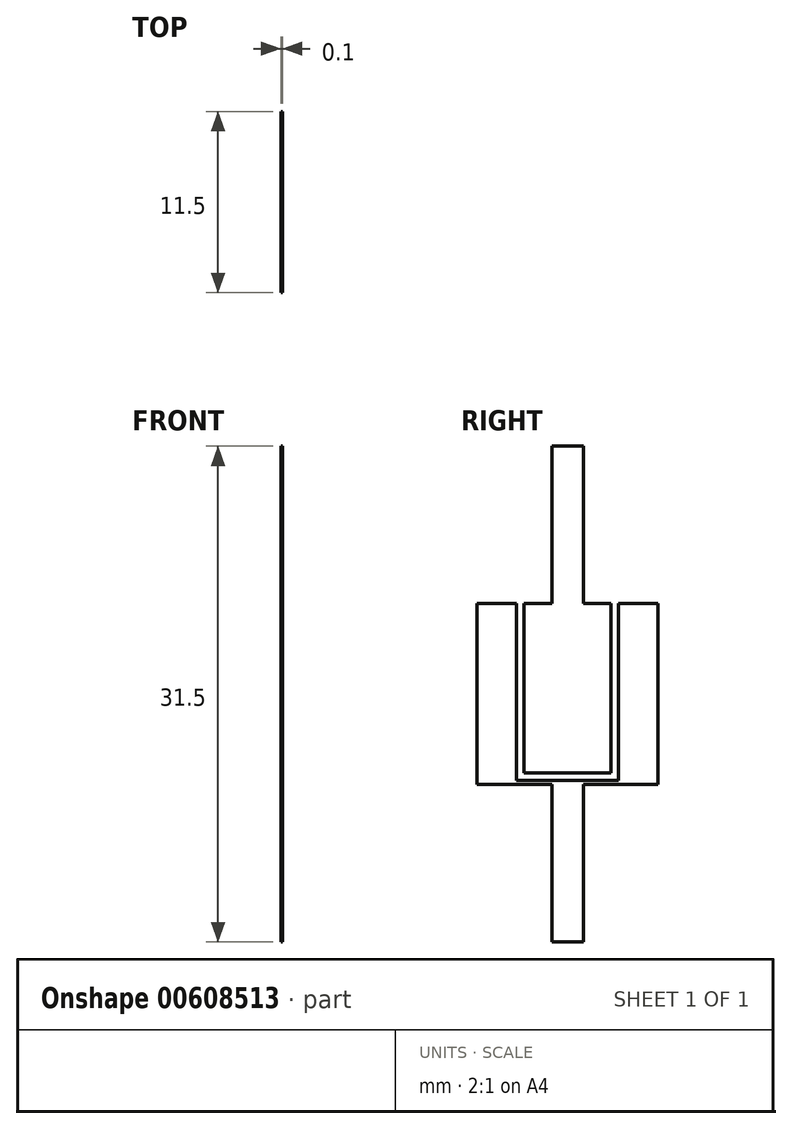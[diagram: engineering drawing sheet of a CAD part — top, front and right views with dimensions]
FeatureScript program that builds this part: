
annotation { "Feature Type Name" : "Feature", "Feature Type Description" : "" }
export const myFeature = defineFeature(function(context is Context, id is Id, definition is map)
    precondition{}
    {
        {
            var Q0;
            Q0=qCreatedBy(makeId("Right.planeOp"),FACE);
            var sketch = newSketch(context, id + "F0", { "sketchPlane" : qUnion([Q0])});
            skLineSegment(sketch, "E0", {"start": v(0, 0) * mm, "end": v(2.5, 0) * mm});
            skLineSegment(sketch, "E1", {"start": v(0, 0) * mm, "end": v(0, -11.5) * mm});
            skLineSegment(sketch, "E2", {"start": v(0, -11.5) * mm, "end": v(4.75, -11.5) * mm});
            skLineSegment(sketch, "E3", {"start": v(11.5, -11.5) * mm, "end": v(11.5, 0) * mm});
            skLineSegment(sketch, "E4", {"start": v(11.5, 0) * mm, "end": v(9, 0) * mm});
            skLineSegment(sketch, "E5.0", {"start": v(9, -9) * mm, "end": v(9, 0) * mm});
            skLineSegment(sketch, "E5.2", {"start": v(2.5, 0) * mm, "end": v(2.5, -9) * mm});
            skLineSegment(sketch, "E6.0", {"start": v(4.75, -11.5) * mm, "end": v(4.75, -21.5) * mm});
            skLineSegment(sketch, "E7.0", {"start": v(6.75, -11.5) * mm, "end": v(6.75, -21.5) * mm});
            skLineSegment(sketch, "E8.trimOffspring", {"start": v(6.75, -11.5) * mm, "end": v(11.5, -11.5) * mm});
            skLineSegment(sketch, "E9", {"start": v(4.75, -21.5) * mm, "end": v(6.75, -21.5) * mm});
            skLineSegment(sketch, "E10.0", {"start": v(3, 0) * mm, "end": v(3, -8.5) * mm});
            skLineSegment(sketch, "E11.0", {"start": v(8.5, -8.5) * mm, "end": v(8.5, 0) * mm});
            skLineSegment(sketch, "E12", {"start": v(3, 0) * mm, "end": v(4.75, 0) * mm});
            skLineSegment(sketch, "E13.0", {"start": v(6.75, 0) * mm, "end": v(6.75, 10) * mm});
            skLineSegment(sketch, "E14.0", {"start": v(4.75, 0) * mm, "end": v(4.75, 10) * mm});
            skLineSegment(sketch, "E15", {"start": v(4.75, 10) * mm, "end": v(6.75, 10) * mm});
            skLineSegment(sketch, "E16.trimOffspring", {"start": v(6.75, 0) * mm, "end": v(8.5, 0) * mm});
            skLineSegment(sketch, "E17", {"start": v(11.5, -11.5) * mm, "end": v(6.75, -11.5) * mm});
            skLineSegment(sketch, "E18.0", {"start": v(9, -11.25) * mm, "end": v(2.5, -11.25) * mm});
            skLineSegment(sketch, "E19", {"start": v(9, -9) * mm, "end": v(9, -11.25) * mm});
            skLineSegment(sketch, "E20", {"start": v(2.5, -9) * mm, "end": v(2.5, -11.25) * mm});
            skLineSegment(sketch, "E21.0", {"start": v(8.5, -10.75) * mm, "end": v(3, -10.75) * mm});
            skLineSegment(sketch, "E22", {"start": v(8.5, -8.5) * mm, "end": v(8.5, -10.75) * mm});
            skLineSegment(sketch, "E23", {"start": v(3, -8.5) * mm, "end": v(3, -10.75) * mm});
            skLineSegment(sketch, "E24.trimOffspring", {"start": v(4.75, -11.5) * mm, "end": v(0, -11.5) * mm});
            skSolve(sketch);
        }
        {
            var Q0;
            Q0=makeQuery(id+"F0.imprint","IMPRINT",FACE,{"disambiguationData":[TD([[makeQuery(id+"F0.imprint","IMPRINT",EDGE,{"derivedFrom":sQuery(id+"F0.wireOp",EDGE,"b56e8115-747c-47a9-926b-84bb7afac1cf.0")}),1.0]])]});
            var Q1;
            Q1=makeQuery(id+"F0.imprint","IMPRINT",FACE,{"disambiguationData":[TD([[makeQuery(id+"F0.imprint","IMPRINT",EDGE,{"derivedFrom":sQuery(id+"F0.wireOp",EDGE,"E0")}),-1.0]])]});
            var Q2;
            Q2=makeQuery(id+"F0.imprint","IMPRINT",FACE,{"disambiguationData":[TD([[makeQuery(id+"F0.imprint","IMPRINT",EDGE,{"derivedFrom":sQuery(id+"F0.wireOp",EDGE,"E10.0")}),1.0]])]});
            extrude(context, id + "F1", {"entities" : qUnion([Q0, Q1, Q2]), "depth" : .1 * mm, "offsetDistance" : 25 * mm});
        }
    });
